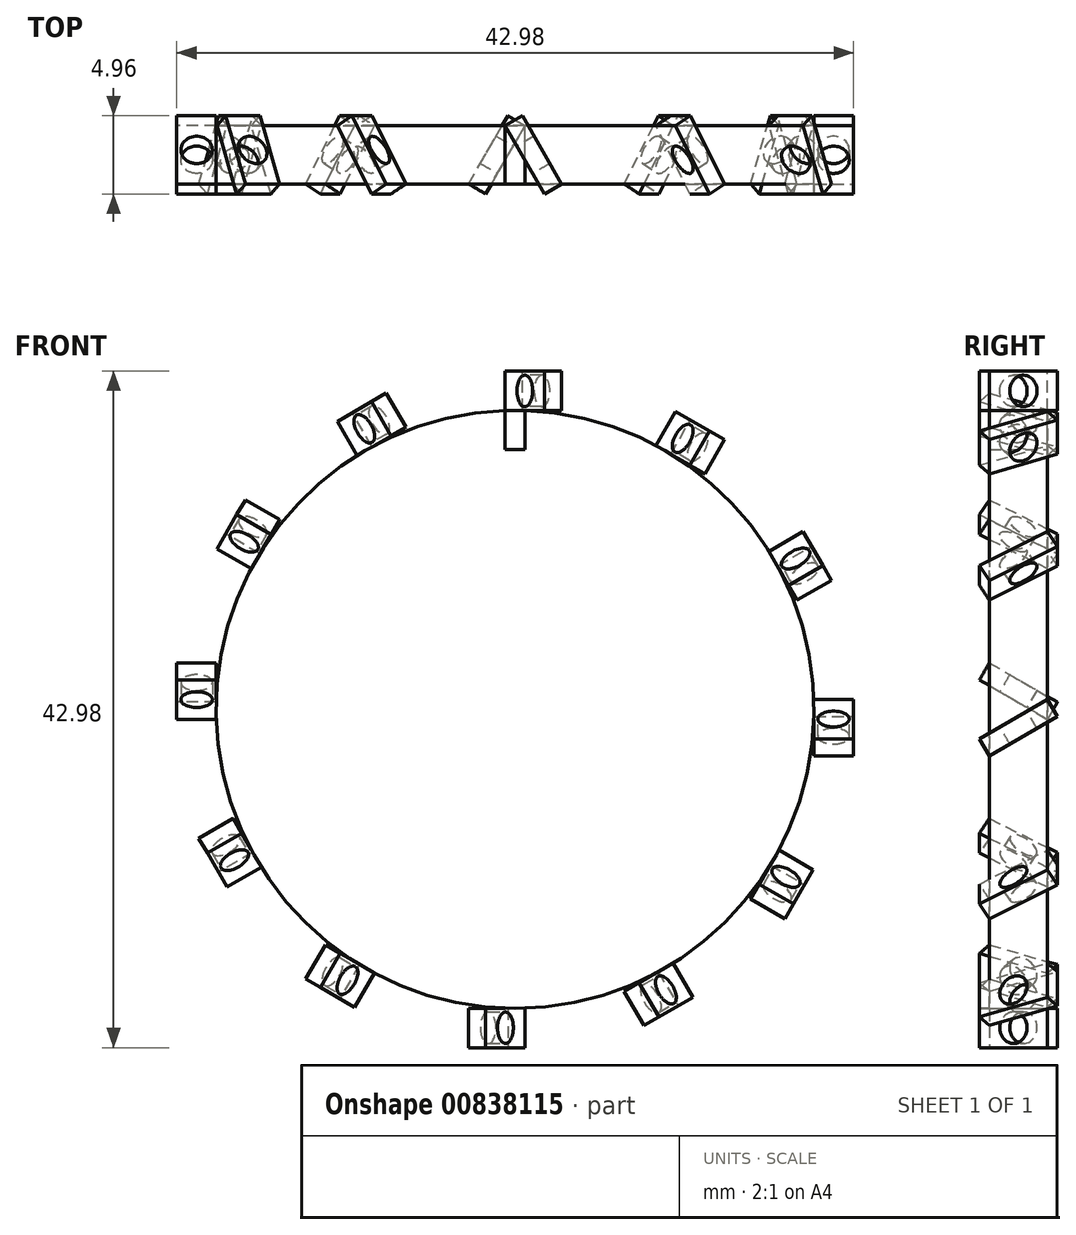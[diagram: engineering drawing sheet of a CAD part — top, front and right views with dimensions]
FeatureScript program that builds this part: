
annotation { "Feature Type Name" : "Feature", "Feature Type Description" : "" }
export const myFeature = defineFeature(function(context is Context, id is Id, definition is map)
    precondition{}
    {
        {
            var Q0;
            Q0=qCreatedBy(makeId("Front.planeOp"),FACE);
            var sketch = newSketch(context, id + "F0", { "sketchPlane" : qUnion([Q0])});
            skCircle(sketch, "E0", {"center": v(-124.3, 44.1) * mm, "radius": 19 * mm});
            skSolve(sketch);
        }
        {
            var Q0;
            Q0=makeQuery(id+"F0.imprint","IMPRINT",FACE,{"disambiguationData":[TD([[makeQuery(id+"F0.imprint","IMPRINT",EDGE,{"derivedFrom":sQuery(id+"F0.wireOp",EDGE,"E0")}),1.0]])]});
            var sketch = newSketch(context, id + "F1", { "sketchPlane" : qUnion([Q0])});
            skLineSegment(sketch, "E1", {"start": v(-124.31, 44.12) * mm, "end": v(-124.31, 63.1) * mm});
            skLineSegment(sketch, "E2.bottom", {"start": v(-123.68, 60.6) * mm, "end": v(-124.94, 60.6) * mm});
            skLineSegment(sketch, "E2.top", {"start": v(-123.68, 65.58) * mm, "end": v(-124.94, 65.58) * mm});
            skLineSegment(sketch, "E2.left", {"start": v(-123.68, 60.6) * mm, "end": v(-123.68, 65.58) * mm});
            skLineSegment(sketch, "E2.right", {"start": v(-124.94, 60.6) * mm, "end": v(-124.94, 65.58) * mm});
            skPoint(sketch, "E2.middle", {"position": v(-124.31, 63.1) * mm});
            skSolve(sketch);
        }
        {
            var Q0;
            {var subQ5=sQuery(id+"F1.wireOp",EDGE,"E2.top");Q0=makeQuery(id+"F1.imprint","IMPRINT",FACE,{"disambiguationData":[TD([[makeQuery(id+"F1.imprint","IMPRINT",EDGE,{"derivedFrom":subQ5}),1.0]])]});}
            extrude(context, id + "F2", {"entities" : qUnion([Q0]), "depth" : 5 * mm, "offsetDistance" : 25 * mm});
        }
        {
            var Q0;
            Q0=makeQuery(id+"F2.opExtrude","SWEPT_BODY",BODY,{"disambiguationData":[OSD([sQuery(id+"F0.wireOp",EDGE,"E0"),sQuery(id+"F1.wireOp",EDGE,"E2.top"),sQuery(id+"F1.wireOp",EDGE,"E2.left"),sQuery(id+"F1.wireOp",EDGE,"E2.right")])]});
            var Q1;
            Q1=makeQuery(id+"F2.opExtrude","CAP_EDGE",EDGE,{"disambiguationData":[OSD([sQuery(id+"F1.wireOp",EDGE,"E2.right")])],"isStart":true});
            transform(context, id + "F3", {"entities" : qUnion([Q0]), "transformType" : TransformType.ROTATION, "transformAxis" : qUnion([Q1]), "angle" : 30 * degree, "makeCopy" : false});
        }
        {
            var Q0;
            Q0=makeQuery(id+"F2.opExtrude","SWEPT_FACE",FACE,{"disambiguationData":[OSD([sQuery(id+"F1.wireOp",EDGE,"E2.right")])]});
            var sketch = newSketch(context, id + "F4", { "sketchPlane" : qUnion([Q0])});
            skPoint(sketch, "E3", {"position": v(-59.97, 64.31) * mm});
            skPoint(sketch, "E3.positionSnap0", {"position": v(-59.97, 65.58) * mm});
            skSolve(sketch);
        }
        {
            var Q0;
            Q0=sQuery(id+"F4.wireOp",VERTEX,"E3");
            var Q1;
            Q1=makeQuery(id+"F2.opExtrude","SWEPT_BODY",BODY,{"disambiguationData":[OSD([sQuery(id+"F0.wireOp",EDGE,"E0"),sQuery(id+"F1.wireOp",EDGE,"E2.top"),sQuery(id+"F1.wireOp",EDGE,"E2.left"),sQuery(id+"F1.wireOp",EDGE,"E2.right")])]});
            hole(context, id + "F5", {"style" : HoleStyle.SIMPLE, "endStyle" : HoleEndStyle.THROUGH, "holeDiameter" : 2 * mm, "majorDiameter" : 5 * mm, "isTappedThrough" : true, "tappedDepth" : 12 * mm, "tapClearance" : 3, "locations" : qUnion([Q0]), "scope" : qUnion([Q1])});
        }
        {
            var Q0;
            Q0=makeQuery(id+"F2.opExtrude","SWEPT_BODY",BODY,{"disambiguationData":[OSD([sQuery(id+"F0.wireOp",EDGE,"E0"),sQuery(id+"F1.wireOp",EDGE,"E2.top"),sQuery(id+"F1.wireOp",EDGE,"E2.left"),sQuery(id+"F1.wireOp",EDGE,"E2.right")])]});
            var Q1;
            Q1=sQuery(id+"F0.wireOp",EDGE,"E0");
            circularPattern(context, id + "F6", {"entities" : qUnion([Q0]), "axis" : qUnion([Q1]), "angle" : 360 * degree, "instanceCount" : 12, "equalSpace" : true});
        }
        {
            var Q0;
            {var subQ0=sQuery(id+"F1.wireOp",EDGE,"E2.left");var subQ1=sQuery(id+"F1.wireOp",EDGE,"E2.bottom");var subQ2=makeQuery(id+"F1.imprint","INTERSECT",VERTEX,{"derivedFrom":[subQ1,subQ0]});Q0=makeQuery(id+"F1.imprint","IMPRINT",FACE,{"disambiguationData":[TD([[makeQuery(id+"F1.imprint","IMPRINT",EDGE,{"disambiguationData":[TD([[subQ2,-1.0]])],"derivedFrom":subQ1}),1.0]])]});}
            extrude(context, id + "F7", {"entities" : qUnion([Q0]), "depth" : 3.7 * mm, "offsetDistance" : 25 * mm});
        }
    });
